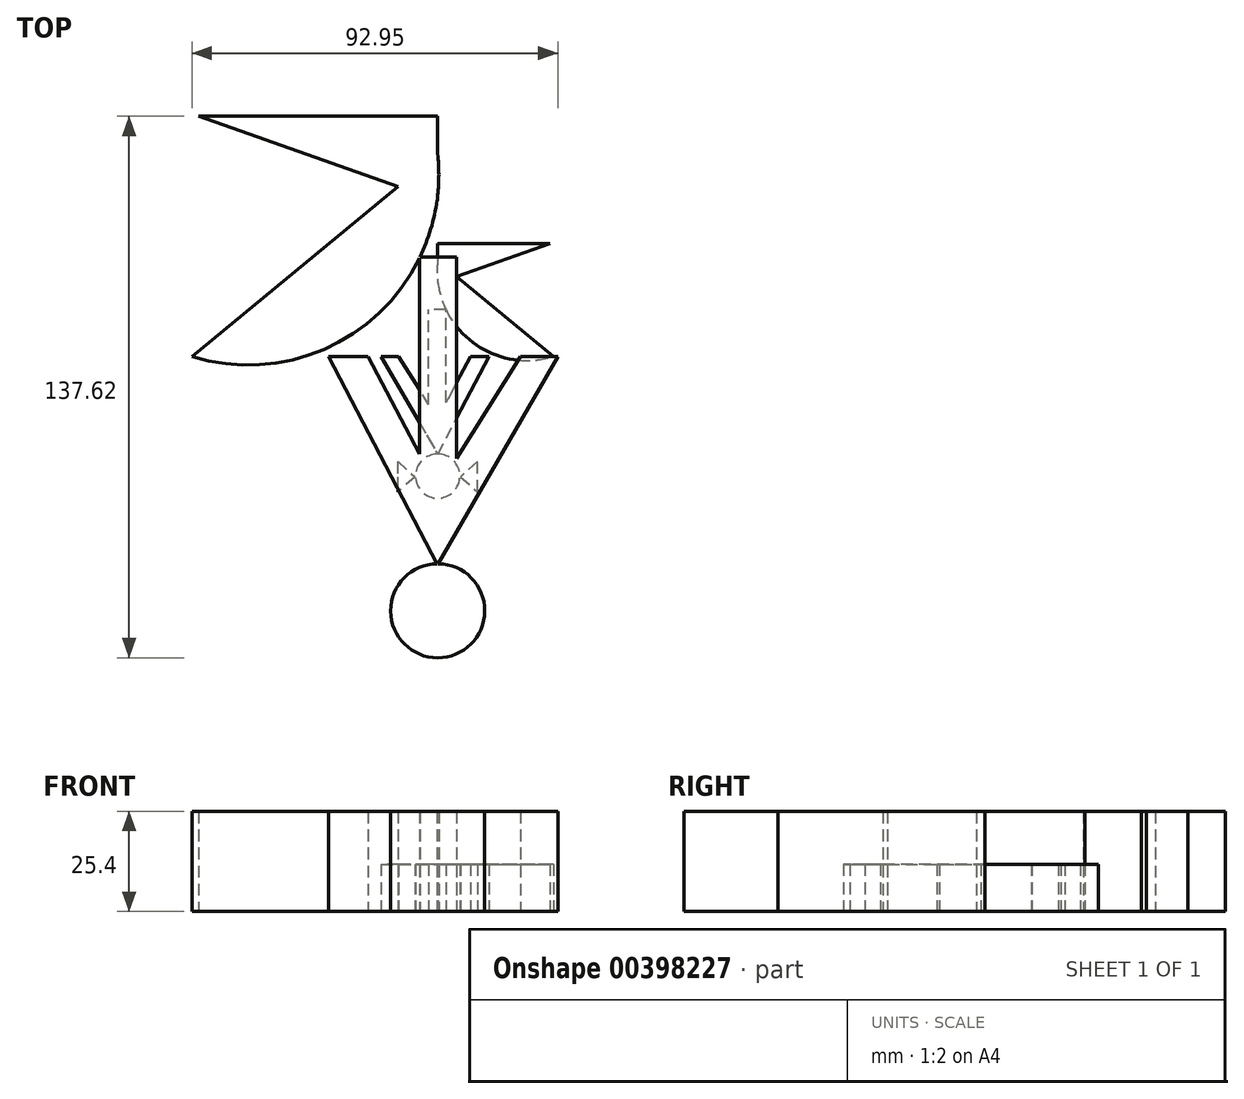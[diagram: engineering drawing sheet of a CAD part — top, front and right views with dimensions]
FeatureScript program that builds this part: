
annotation { "Feature Type Name" : "Feature", "Feature Type Description" : "" }
export const myFeature = defineFeature(function(context is Context, id is Id, definition is map)
    precondition{}
    {
        {
            var Q0;
            Q0=qCreatedBy(makeId("Top.planeOp"),FACE);
            var sketch = newSketch(context, id + "F0", { "sketchPlane" : qUnion([Q0])});
            skLineSegment(sketch, "E0", {"start": v(-30.52, 0) * mm, "end": v(0, -52.88) * mm});
            skLineSegment(sketch, "E1", {"start": v(0, -52.88) * mm, "end": v(27.71, 0) * mm});
            skLineSegment(sketch, "E2", {"start": v(27.71, 0) * mm, "end": v(17.65, 0) * mm});
            skLineSegment(sketch, "E3", {"start": v(17.65, 0) * mm, "end": v(0, -33.68) * mm});
            skLineSegment(sketch, "E4", {"start": v(0, -33.68) * mm, "end": v(-21.1, 0) * mm});
            skLineSegment(sketch, "E5", {"start": v(-21.1, 0) * mm, "end": v(-30.52, 0) * mm});
            skSolve(sketch);
        }
        {
            var Q0;
            Q0 = qSketchRegion(id + "F0", true);
            extrude(context, id + "F1", {"entities" : qUnion([Q0]), "depth" : 25.4 * mm});
        }
        {
            var Q0;
            Q0=qCreatedBy(makeId("Top.planeOp"),FACE);
            var sketch = newSketch(context, id + "F2", { "sketchPlane" : qUnion([Q0])});
            skCircle(sketch, "E6", {"center": v(0, -64.61) * mm, "radius": 11.96 * mm});
            skSolve(sketch);
        }
        {
            var Q0;
            Q0 = qSketchRegion(id + "F2", true);
            extrude(context, id + "F3", {"entities" : qUnion([Q0]), "operationType" : NewBodyOperationType.ADD, "depth" : 25.4 * mm});
        }
        {
            var Q0;
            Q0=qCreatedBy(makeId("Top.planeOp"),FACE);
            var sketch = newSketch(context, id + "F4", { "sketchPlane" : qUnion([Q0])});
            skLineSegment(sketch, "E7.bottom", {"start": v(4.63, -34.52) * mm, "end": v(-4.82, -34.52) * mm});
            skLineSegment(sketch, "E7.top", {"start": v(4.63, 25.29) * mm, "end": v(-4.82, 25.29) * mm});
            skLineSegment(sketch, "E7.left", {"start": v(4.63, -34.52) * mm, "end": v(4.63, 25.29) * mm});
            skLineSegment(sketch, "E7.right", {"start": v(-4.82, -34.52) * mm, "end": v(-4.82, 25.29) * mm});
            skSolve(sketch);
        }
        {
            var Q0;
            Q0 = qSketchRegion(id + "F4", true);
            extrude(context, id + "F5", {"entities" : qUnion([Q0]), "operationType" : NewBodyOperationType.ADD, "depth" : 25.4 * mm});
        }
        {
            var Q0;
            Q0=qCreatedBy(makeId("Top.planeOp"),FACE);
            var sketch = newSketch(context, id + "F6", { "sketchPlane" : qUnion([Q0])});
            skCircle(sketch, "E8", {"center": v(0, -73.79) * mm, "radius": 1.86 * mm});
            skSolve(sketch);
        }
        {
            var Q0;
            Q0 = qSketchRegion(id + "F6", true);
            extrude(context, id + "F7", {"entities" : qUnion([Q0]), "operationType" : NewBodyOperationType.REMOVE, "endBound" : BoundingType.THROUGH_ALL, "oppositeDirection" : true, "depth" : 76.2 * mm});
        }
        {
            var Q0;
            Q0=qCreatedBy(makeId("Top.planeOp"),FACE);
            var sketch = newSketch(context, id + "F8", { "sketchPlane" : qUnion([Q0])});
            skLineSegment(sketch, "E9", {"start": v(12.35, -65.04) * mm, "end": v(21.51, -73.1) * mm});
            skLineSegment(sketch, "E10", {"start": v(21.51, -73.1) * mm, "end": v(21.51, -56.7) * mm});
            skLineSegment(sketch, "E11", {"start": v(21.51, -56.7) * mm, "end": v(12.35, -65.04) * mm});
            skSolve(sketch);
        }
        {
            var Q0;
            Q0 = qSketchRegion(id + "F8", true);
            extrude(context, id + "F9", {"entities" : qUnion([Q0]), "depth" : 25.4 * mm});
        }
        {
            var Q0;
            Q0=makeQuery(id+"F9.opExtrude","SWEPT_BODY",BODY,{"disambiguationData":[OSD([sQuery(id+"F8.wireOp",EDGE,"E9"),sQuery(id+"F8.wireOp",EDGE,"E10"),sQuery(id+"F8.wireOp",EDGE,"E11")])]});
            var Q1;
            Q1=qCreatedBy(makeId("Right.planeOp"),FACE);
            mirror(context, id + "F10", {"entities" : qUnion([Q0]), "mirrorPlane" : qUnion([Q1])});
        }
        {
            var Q0;
            Q0=qCreatedBy(makeId("Top.planeOp"),FACE);
            var sketch = newSketch(context, id + "F11", { "sketchPlane" : qUnion([Q0])});
            skArc(sketch, "E12", {"start": v(0, 51.5) * mm, "mid": v(17.31, 8.9) * mm, "end": v(62.43, 0) * mm});
            skLineSegment(sketch, "E13", {"start": v(62.43, 0) * mm, "end": v(0, 51.5) * mm});
            skSolve(sketch);
        }
        {
            var Q0;
            Q0 = qSketchRegion(id + "F11", true);
            extrude(context, id + "F12", {"entities" : qUnion([Q0]), "operationType" : NewBodyOperationType.ADD, "depth" : 25.4 * mm});
        }
        {
            var Q0;
            Q0=qCreatedBy(makeId("Top.planeOp"),FACE);
            var sketch = newSketch(context, id + "F13", { "sketchPlane" : qUnion([Q0])});
            skLineSegment(sketch, "E14", {"start": v(0, 39.64) * mm, "end": v(60.76, 61.05) * mm});
            skLineSegment(sketch, "E15", {"start": v(60.76, 61.05) * mm, "end": v(0, 61.05) * mm});
            skLineSegment(sketch, "E16", {"start": v(0, 61.05) * mm, "end": v(0, 39.64) * mm});
            skSolve(sketch);
        }
        {
            var Q0;
            Q0 = qSketchRegion(id + "F13", true);
            extrude(context, id + "F14", {"entities" : qUnion([Q0]), "operationType" : NewBodyOperationType.ADD, "depth" : 25.4 * mm});
        }
        {
            var Q0;
            Q0=makeQuery(id+"F1.opExtrude","SWEPT_BODY",BODY,{"disambiguationData":[OSD([sQuery(id+"F0.wireOp",EDGE,"E0"),sQuery(id+"F0.wireOp",EDGE,"E1"),sQuery(id+"F0.wireOp",EDGE,"E2"),sQuery(id+"F0.wireOp",EDGE,"E3"),sQuery(id+"F0.wireOp",EDGE,"E4"),sQuery(id+"F0.wireOp",EDGE,"E5")])]});
            var Q1;
            Q1=qCreatedBy(makeId("Right.planeOp"),FACE);
            mirror(context, id + "F15", {"operationType" : NewBodyOperationType.ADD, "entities" : qUnion([Q0]), "mirrorPlane" : qUnion([Q1])});
        }
        {
            var Q0;
            Q0=makeQuery(id+"F1.opExtrude","SWEPT_BODY",BODY,{"disambiguationData":[OSD([sQuery(id+"F0.wireOp",EDGE,"E0"),sQuery(id+"F0.wireOp",EDGE,"E1"),sQuery(id+"F0.wireOp",EDGE,"E2"),sQuery(id+"F0.wireOp",EDGE,"E3"),sQuery(id+"F0.wireOp",EDGE,"E4"),sQuery(id+"F0.wireOp",EDGE,"E5")])]});
            var Q1;
            Q1=makeQuery(id+"F9.opExtrude","SWEPT_BODY",BODY,{"disambiguationData":[OSD([sQuery(id+"F8.wireOp",EDGE,"E9"),sQuery(id+"F8.wireOp",EDGE,"E10"),sQuery(id+"F8.wireOp",EDGE,"E11")])]});
            var Q2;
            Q2=makeQuery(id+"F10.opPattern","COPY",BODY,{"derivedFrom":makeQuery(id+"F9.opExtrude","SWEPT_BODY",BODY,{"disambiguationData":[OSD([sQuery(id+"F8.wireOp",EDGE,"E9"),sQuery(id+"F8.wireOp",EDGE,"E10"),sQuery(id+"F8.wireOp",EDGE,"E11")])]}),"instanceName":"1"});
            var Q3;
            Q3=qCreatedBy(makeId("Origin.pointOp"),VERTEX);
            transform(context, id + "F16", {"entities" : qUnion([Q0, Q1, Q2]), "transformType" : TransformType.SCALE_UNIFORMLY, "scale" : 0.47, "scalePoint" : qUnion([Q3]), "makeCopy" : false});
        }
    });
